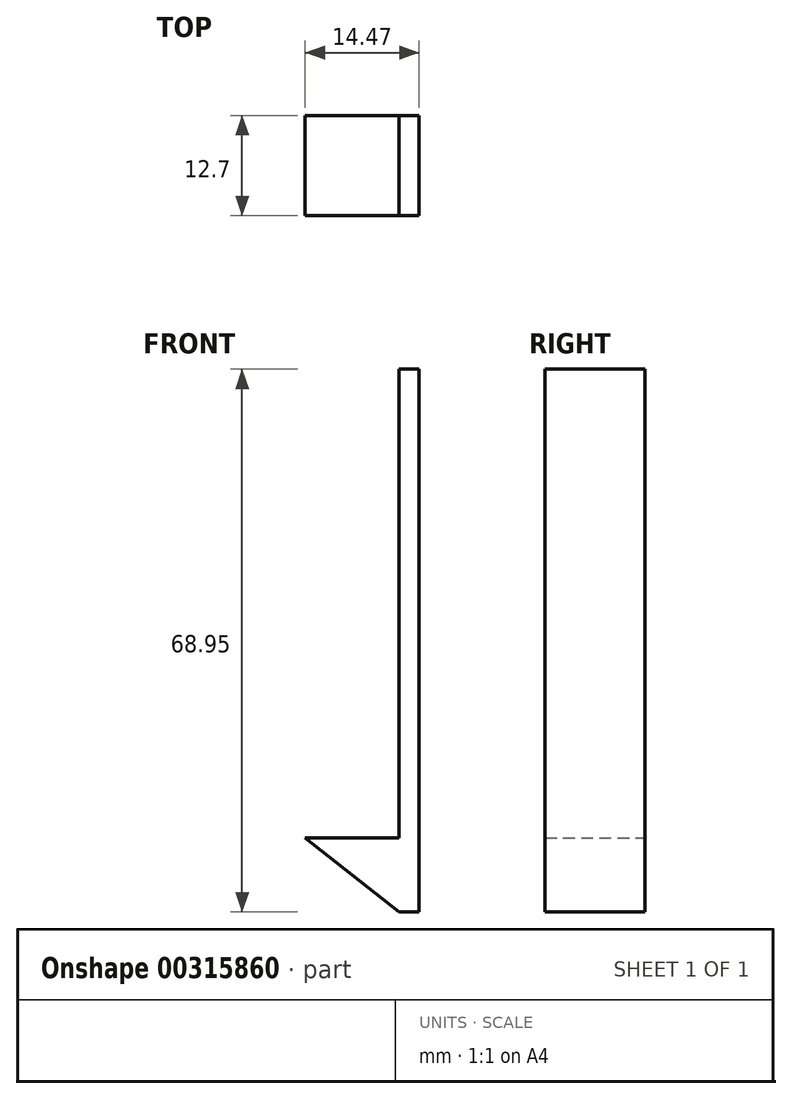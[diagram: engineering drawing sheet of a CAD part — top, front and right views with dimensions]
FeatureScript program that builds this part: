
annotation { "Feature Type Name" : "Feature", "Feature Type Description" : "" }
export const myFeature = defineFeature(function(context is Context, id is Id, definition is map)
    precondition{}
    {
        {
            var Q0;
            Q0=qCreatedBy(makeId("Front.planeOp"),FACE);
            var sketch = newSketch(context, id + "F0", { "sketchPlane" : qUnion([Q0])});
            skLineSegment(sketch, "E0", {"start": v(0, 41.3) * mm, "end": v(0, -18.25) * mm});
            skLineSegment(sketch, "E1", {"start": v(0, -18.25) * mm, "end": v(0, -27.65) * mm});
            skLineSegment(sketch, "E2", {"start": v(0, -27.65) * mm, "end": v(2.58, -27.65) * mm});
            skLineSegment(sketch, "E3", {"start": v(2.58, -27.65) * mm, "end": v(2.58, 41.3) * mm});
            skLineSegment(sketch, "E4", {"start": v(0, 41.3) * mm, "end": v(2.58, 41.3) * mm});
            skLineSegment(sketch, "E5", {"start": v(0, -18.25) * mm, "end": v(-11.9, -18.25) * mm});
            skLineSegment(sketch, "E6", {"start": v(0, -27.65) * mm, "end": v(-11.9, -18.25) * mm});
            skSolve(sketch);
        }
        {
            var Q0;
            Q0 = qSketchRegion(id + "F0", true);
            extrude(context, id + "F1", {"entities" : qUnion([Q0]), "depth" : 12.7 * mm});
        }
    });
